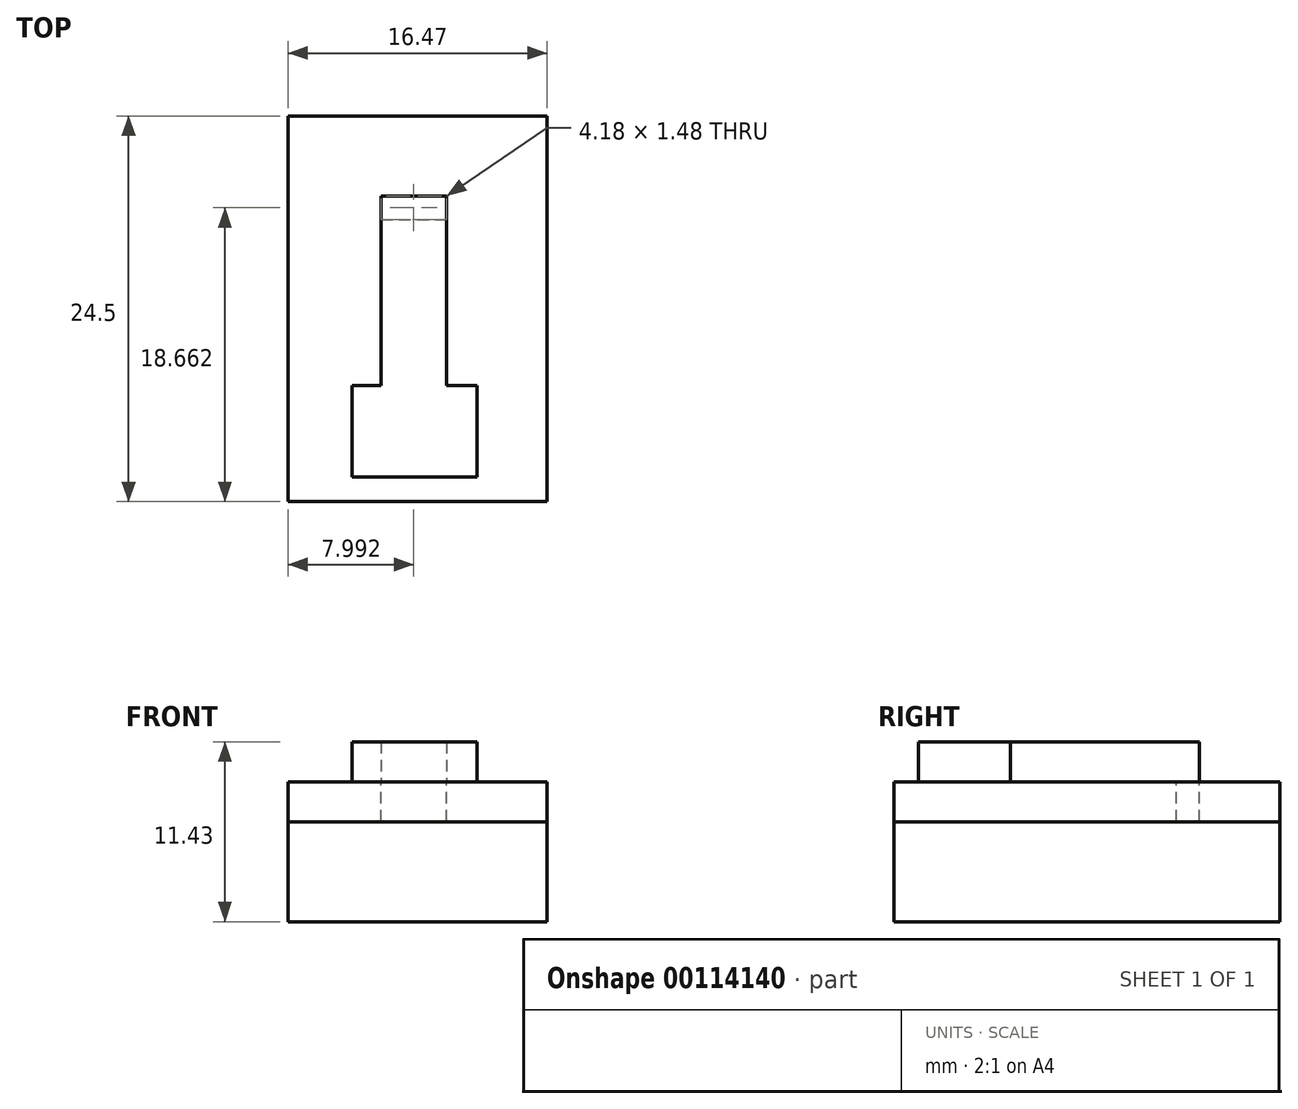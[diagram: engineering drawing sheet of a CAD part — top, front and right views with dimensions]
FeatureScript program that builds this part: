
annotation { "Feature Type Name" : "Feature", "Feature Type Description" : "" }
export const myFeature = defineFeature(function(context is Context, id is Id, definition is map)
    precondition{}
    {
        {
            var Q0;
            Q0=qCreatedBy(makeId("Top.planeOp"),FACE);
            var sketch = newSketch(context, id + "F0", { "sketchPlane" : qUnion([Q0])});
            skLineSegment(sketch, "E0.bottom", {"start": v(-7.99, 12.48) * mm, "end": v(8.48, 12.48) * mm});
            skLineSegment(sketch, "E0.top", {"start": v(-7.99, -12.02) * mm, "end": v(8.48, -12.02) * mm});
            skLineSegment(sketch, "E0.left", {"start": v(-7.99, 12.48) * mm, "end": v(-7.99, -12.02) * mm});
            skLineSegment(sketch, "E0.right", {"start": v(8.48, 12.48) * mm, "end": v(8.48, -12.02) * mm});
            skSolve(sketch);
        }
        {
            var Q0;
            Q0=makeQuery(id+"F0.imprint","IMPRINT",FACE,{"disambiguationData":[TD([[makeQuery(id+"F0.imprint","IMPRINT",EDGE,{"derivedFrom":sQuery(id+"F0.wireOp",EDGE,"E0.bottom")}),-1.0]])]});
            extrude(context, id + "F1", {"entities" : qUnion([Q0]), "depth" : 6.35 * mm});
        }
        {
            var Q0;
            Q0=makeQuery(id+"F1.opExtrude","CAP_FACE",FACE,{"disambiguationData":[OSD([sQuery(id+"F0.wireOp",EDGE,"E0.bottom"),sQuery(id+"F0.wireOp",EDGE,"E0.top"),sQuery(id+"F0.wireOp",EDGE,"E0.left"),sQuery(id+"F0.wireOp",EDGE,"E0.right")])],"isStart":false});
            var sketch = newSketch(context, id + "F2", { "sketchPlane" : qUnion([Q0])});
            skLineSegment(sketch, "E1.bottom", {"start": v(-7.99, 12.48) * mm, "end": v(8.48, 12.48) * mm});
            skLineSegment(sketch, "E1.top", {"start": v(-7.99, -12.02) * mm, "end": v(8.48, -12.02) * mm});
            skLineSegment(sketch, "E1.left", {"start": v(-7.99, 12.48) * mm, "end": v(-7.99, -12.02) * mm});
            skLineSegment(sketch, "E1.right", {"start": v(8.48, 12.48) * mm, "end": v(8.48, -12.02) * mm});
            skSolve(sketch);
        }
        {
            var Q0;
            Q0=qSketchRegion(id+"F2",true);
            var Q1;
            Q1=qSketchRegion(id+"F4",true);
            extrude(context, id + "F3", {"entities" : qUnion([Q0, Q1]), "depth" : 2.54 * mm});
        }
        {
            var Q0;
            Q0=makeQuery(id+"F3.opExtrude","CAP_FACE",FACE,{"disambiguationData":[OSD([sQuery(id+"F2.wireOp",EDGE,"E1.bottom"),sQuery(id+"F2.wireOp",EDGE,"E1.top"),sQuery(id+"F2.wireOp",EDGE,"E1.left"),sQuery(id+"F2.wireOp",EDGE,"E1.right")])],"isStart":false});
            var sketch = newSketch(context, id + "F4", { "sketchPlane" : qUnion([Q0])});
            skLineSegment(sketch, "E2.bottom", {"start": v(-2.09, 7.38) * mm, "end": v(2.1, 7.38) * mm});
            skLineSegment(sketch, "E2.top", {"start": v(-2.09, 5.9) * mm, "end": v(2.1, 5.9) * mm});
            skLineSegment(sketch, "E2.left", {"start": v(-2.09, 7.38) * mm, "end": v(-2.09, 5.9) * mm});
            skLineSegment(sketch, "E2.right", {"start": v(2.1, 7.38) * mm, "end": v(2.1, 5.9) * mm});
            skSolve(sketch);
        }
        {
            var Q0;
            Q0=qSketchRegion(id+"F4",true);
            extrude(context, id + "F5", {"entities" : qUnion([Q0]), "operationType" : NewBodyOperationType.REMOVE, "oppositeDirection" : true, "depth" : 2.54 * mm});
        }
        {
            var Q0;
            Q0=makeQuery(id+"F3.opExtrude","CAP_FACE",FACE,{"disambiguationData":[OSD([sQuery(id+"F2.wireOp",EDGE,"E1.bottom"),sQuery(id+"F2.wireOp",EDGE,"E1.top"),sQuery(id+"F2.wireOp",EDGE,"E1.left"),sQuery(id+"F2.wireOp",EDGE,"E1.right")])],"isStart":false});
            var sketch = newSketch(context, id + "F6", { "sketchPlane" : qUnion([Q0])});
            skLineSegment(sketch, "E3.bottom", {"start": v(-2.09, 7.38) * mm, "end": v(2.1, 7.38) * mm});
            skLineSegment(sketch, "E3.top", {"start": v(-2.09, -10.45) * mm, "end": v(2.1, -10.45) * mm});
            skLineSegment(sketch, "E3.left", {"start": v(-2.09, 7.38) * mm, "end": v(-2.09, -10.45) * mm});
            skLineSegment(sketch, "E3.right", {"start": v(2.1, 7.38) * mm, "end": v(2.1, -10.45) * mm});
            skLineSegment(sketch, "E4.bottom", {"start": v(-3.92, -4.64) * mm, "end": v(4, -4.64) * mm});
            skLineSegment(sketch, "E4.top", {"start": v(-3.92, -10.47) * mm, "end": v(4, -10.47) * mm});
            skLineSegment(sketch, "E4.left", {"start": v(-3.92, -4.64) * mm, "end": v(-3.92, -10.47) * mm});
            skLineSegment(sketch, "E4.right", {"start": v(4, -4.64) * mm, "end": v(4, -10.47) * mm});
            skSolve(sketch);
        }
        {
            var Q0;
            Q0=qSketchRegion(id+"F6",true);
            extrude(context, id + "F7", {"entities" : qUnion([Q0]), "depth" : 2.54 * mm});
        }
    });
